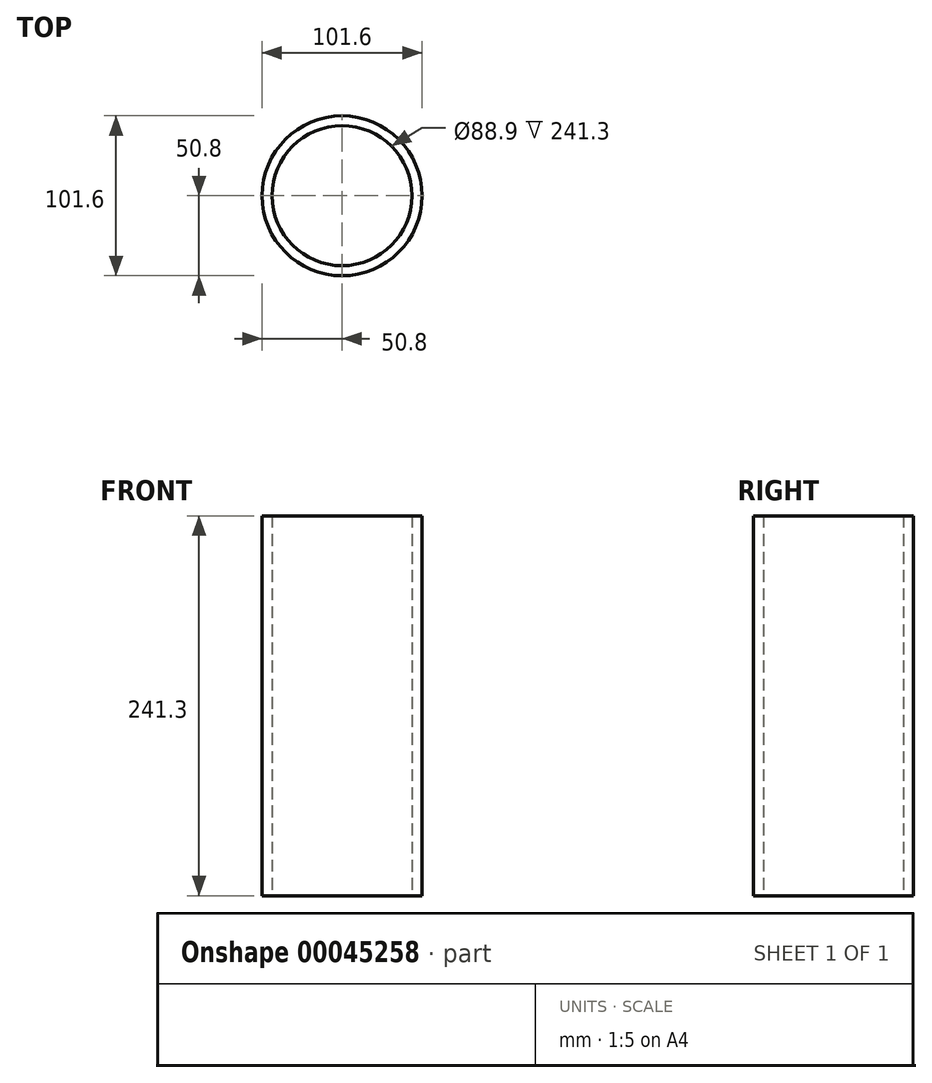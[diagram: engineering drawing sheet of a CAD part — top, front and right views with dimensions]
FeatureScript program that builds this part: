
annotation { "Feature Type Name" : "Feature", "Feature Type Description" : "" }
export const myFeature = defineFeature(function(context is Context, id is Id, definition is map)
    precondition{}
    {
        {
            var Q0;
            Q0=qCreatedBy(makeId("Top.planeOp"),FACE);
            var sketch = newSketch(context, id + "F0", { "sketchPlane" : qUnion([Q0])});
            skCircle(sketch, "E0", {"center": v(0, 0) * mm, "radius": 50.8 * mm});
            skCircle(sketch, "E1", {"center": v(0, 0) * mm, "radius": 44.45 * mm});
            skSolve(sketch);
        }
        {
            var Q0;
            Q0 = qSketchRegion(id + "F0", true);
            extrude(context, id + "F1", {"entities" : qUnion([Q0]), "endBound" : BoundingType.SYMMETRIC, "depth" : 241.3 * mm});
        }
    });
